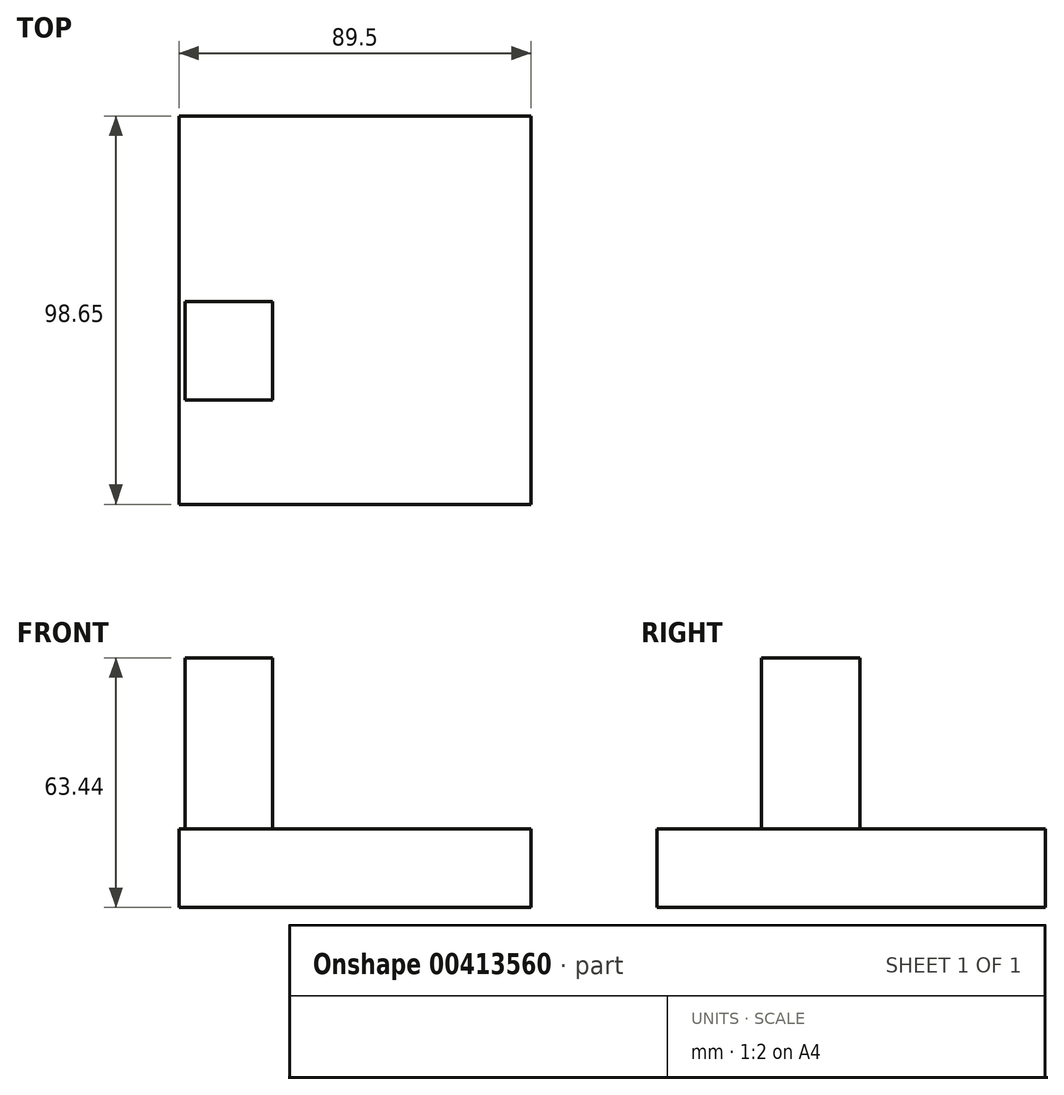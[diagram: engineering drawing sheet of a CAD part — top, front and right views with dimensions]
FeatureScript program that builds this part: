
annotation { "Feature Type Name" : "Feature", "Feature Type Description" : "" }
export const myFeature = defineFeature(function(context is Context, id is Id, definition is map)
    precondition{}
    {
        {
            var Q0;
            Q0=qCreatedBy(makeId("Top.planeOp"),FACE);
            var sketch = newSketch(context, id + "F0", { "sketchPlane" : qUnion([Q0])});
            skLineSegment(sketch, "E0.bottom", {"start": v(-41.7, 47.16) * mm, "end": v(47.8, 47.16) * mm});
            skLineSegment(sketch, "E0.top", {"start": v(-41.7, -51.49) * mm, "end": v(47.8, -51.49) * mm});
            skLineSegment(sketch, "E0.left", {"start": v(-41.7, 47.16) * mm, "end": v(-41.7, -51.49) * mm});
            skLineSegment(sketch, "E0.right", {"start": v(47.8, 47.16) * mm, "end": v(47.8, -51.49) * mm});
            skSolve(sketch);
        }
        {
            var Q0;
            Q0=makeQuery(id+"F0.imprint","IMPRINT",FACE,{"disambiguationData":[TD([[makeQuery(id+"F0.imprint","IMPRINT",EDGE,{"derivedFrom":sQuery(id+"F0.wireOp",EDGE,"E0.bottom")}),-1.0]])]});
            var Q1;
            Q1 = qSketchRegion(id + "F0", true);
            extrude(context, id + "F1", {"entities" : qUnion([Q0, Q1]), "depth" : 20 * mm});
        }
        {
            var Q0;
            Q0=qCreatedBy(makeId("Front.planeOp"),FACE);
            var sketch = newSketch(context, id + "F2", { "sketchPlane" : qUnion([Q0])});
            skLineSegment(sketch, "E1.bottom", {"start": v(-40.1, 63.44) * mm, "end": v(-17.91, 63.44) * mm});
            skLineSegment(sketch, "E1.top", {"start": v(-40.1, 0) * mm, "end": v(-17.91, 0) * mm});
            skLineSegment(sketch, "E1.left", {"start": v(-40.1, 63.44) * mm, "end": v(-40.1, 0) * mm});
            skLineSegment(sketch, "E1.right", {"start": v(-17.91, 63.44) * mm, "end": v(-17.91, 0) * mm});
            skSolve(sketch);
        }
        {
            var Q0;
            Q0 = qSketchRegion(id + "F2", true);
            extrude(context, id + "F3", {"entities" : qUnion([Q0]), "operationType" : NewBodyOperationType.ADD, "depth" : 25 * mm});
        }
    });
